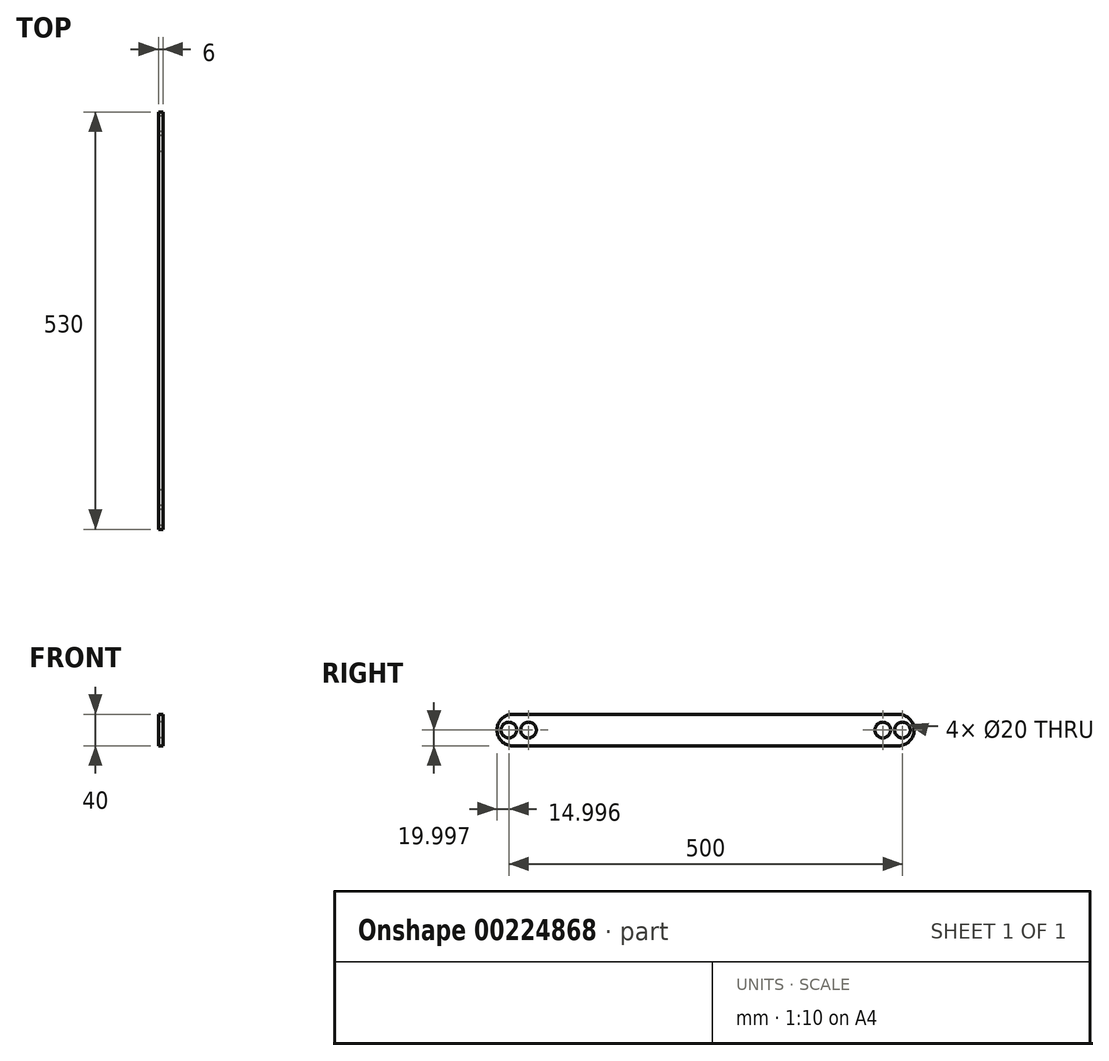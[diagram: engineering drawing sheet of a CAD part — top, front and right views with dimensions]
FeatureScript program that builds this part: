
annotation { "Feature Type Name" : "Feature", "Feature Type Description" : "" }
export const myFeature = defineFeature(function(context is Context, id is Id, definition is map)
    precondition{}
    {
        {
            var Q0;
            Q0=qCreatedBy(makeId("Right.planeOp"),FACE);
            var sketch = newSketch(context, id + "F0", { "sketchPlane" : qUnion([Q0])});
            skLineSegment(sketch, "E0", {"start": v(-152.66, -1.05) * mm, "end": v(337.34, -1.05) * mm});
            skLineSegment(sketch, "E1", {"start": v(357.34, -21.05) * mm, "end": v(357.34, -21.05) * mm});
            skLineSegment(sketch, "E2", {"start": v(337.34, -41.05) * mm, "end": v(-152.66, -41.05) * mm});
            skLineSegment(sketch, "E3", {"start": v(-172.66, -21.05) * mm, "end": v(-172.66, -21.05) * mm});
            skLineSegment(sketch, "E4", {"start": v(-172.66, -21.05) * mm, "end": v(357.34, -21.05) * mm, "construction": true});
            skCircle(sketch, "E5", {"center": v(-157.66, -21.05) * mm, "radius": 10 * mm});
            skCircle(sketch, "E6", {"center": v(-132.66, -21.05) * mm, "radius": 10 * mm});
            skPoint(sketch, "E7.visualSharp", {"position": v(-172.66, -1.05) * mm});
            skArc(sketch, "E7.filletArc", {"start": v(-152.66, -1.05) * mm, "mid": v(-166.8, -6.91) * mm, "end": v(-172.66, -21.05) * mm});
            skPoint(sketch, "E8.visualSharp", {"position": v(-172.66, -41.05) * mm});
            skArc(sketch, "E8.filletArc", {"start": v(-172.66, -21.05) * mm, "mid": v(-166.8, -35.2) * mm, "end": v(-152.66, -41.05) * mm});
            skPoint(sketch, "E9.visualSharp", {"position": v(357.34, -1.05) * mm});
            skArc(sketch, "E9.filletArc", {"start": v(357.34, -21.05) * mm, "mid": v(351.48, -6.91) * mm, "end": v(337.34, -1.05) * mm});
            skPoint(sketch, "E10.visualSharp", {"position": v(357.34, -41.05) * mm});
            skArc(sketch, "E10.filletArc", {"start": v(337.34, -41.05) * mm, "mid": v(351.48, -35.2) * mm, "end": v(357.34, -21.05) * mm});
            skLineSegment(sketch, "E11", {"start": v(92.34, -1.05) * mm, "end": v(92.34, -52.27) * mm, "construction": true});
            skPoint(sketch, "E11.endSnap0", {"position": v(92.34, -41.05) * mm});
            skCircle(sketch, "E12.MirrorC", {"center": v(317.34, -21.05) * mm, "radius": 10 * mm});
            skCircle(sketch, "E13.MirrorC", {"center": v(342.34, -21.05) * mm, "radius": 10 * mm});
            skSolve(sketch);
        }
        {
            var Q0;
            Q0 = qSketchRegion(id + "F0", true);
            extrude(context, id + "F1", {"entities" : qUnion([Q0]), "depth" : 6 * mm});
        }
    });
